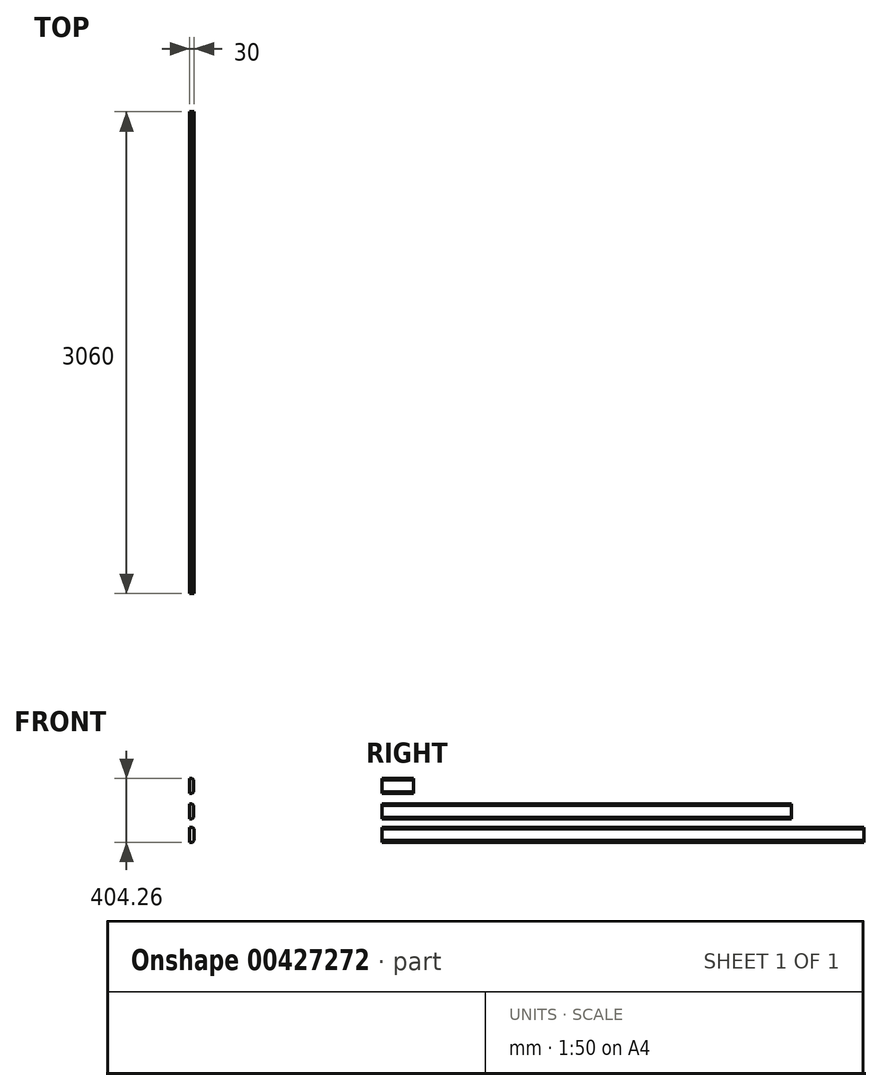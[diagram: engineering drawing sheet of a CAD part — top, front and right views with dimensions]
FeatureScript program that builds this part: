
annotation { "Feature Type Name" : "Feature", "Feature Type Description" : "" }
export const myFeature = defineFeature(function(context is Context, id is Id, definition is map)
    precondition{}
    {
        {
            var Q0;
            Q0=qCreatedBy(makeId("Right.planeOp"),FACE);
            var sketch = newSketch(context, id + "F0", { "sketchPlane" : qUnion([Q0])});
            skLineSegment(sketch, "E0.bottom", {"start": v(0, 0) * mm, "end": v(3060, 0) * mm});
            skLineSegment(sketch, "E0.top", {"start": v(0, 95) * mm, "end": v(3060, 95) * mm});
            skLineSegment(sketch, "E0.left", {"start": v(0, 0) * mm, "end": v(0, 95) * mm});
            skLineSegment(sketch, "E0.right", {"start": v(3060, 0) * mm, "end": v(3060, 95) * mm});
            skSolve(sketch);
        }
        {
            var Q0;
            Q0 = qSketchRegion(id + "F0", true);
            extrude(context, id + "F1", {"entities" : qUnion([Q0]), "depth" : 30 * mm, "offsetDistance" : 25 * mm});
        }
        {
            var Q0;
            Q0=makeQuery(id+"F1.opExtrude","CAP_EDGE",EDGE,{"disambiguationData":[OSD([sQuery(id+"F0.wireOp",EDGE,"E0.top")])],"isStart":false});
            var Q1;
            Q1=makeQuery(id+"F1.opExtrude","CAP_EDGE",EDGE,{"disambiguationData":[OSD([sQuery(id+"F0.wireOp",EDGE,"E0.bottom")])],"isStart":false});
            chamfer(context, id + "F2", {"entities" : qUnion([Q0, Q1]), "width" : 10 * mm, "tangentPropagation" : true});
        }
        {
            var Q0;
            Q0=qCreatedBy(makeId("Right.planeOp"),FACE);
            var sketch = newSketch(context, id + "F3", { "sketchPlane" : qUnion([Q0])});
            skLineSegment(sketch, "E1.bottom", {"start": v(0, 147.75) * mm, "end": v(2600, 147.75) * mm});
            skLineSegment(sketch, "E1.top", {"start": v(0, 242.75) * mm, "end": v(2600, 242.75) * mm});
            skLineSegment(sketch, "E1.left", {"start": v(0, 147.75) * mm, "end": v(0, 242.75) * mm});
            skLineSegment(sketch, "E1.right", {"start": v(2600, 147.75) * mm, "end": v(2600, 242.75) * mm});
            skSolve(sketch);
        }
        {
            var Q0;
            Q0 = qSketchRegion(id + "F3", true);
            extrude(context, id + "F4", {"entities" : qUnion([Q0]), "depth" : 25 * mm, "offsetDistance" : 25 * mm});
        }
        {
            var Q0;
            Q0=makeQuery(id+"F4.opExtrude","CAP_EDGE",EDGE,{"disambiguationData":[OSD([sQuery(id+"F3.wireOp",EDGE,"E1.bottom")])],"isStart":false});
            var Q1;
            Q1=makeQuery(id+"F4.opExtrude","CAP_EDGE",EDGE,{"disambiguationData":[OSD([sQuery(id+"F3.wireOp",EDGE,"E1.top")])],"isStart":false});
            chamfer(context, id + "F5", {"entities" : qUnion([Q0, Q1]), "width" : 10 * mm, "tangentPropagation" : true});
        }
        {
            var Q0;
            Q0=qCreatedBy(makeId("Right.planeOp"),FACE);
            var sketch = newSketch(context, id + "F6", { "sketchPlane" : qUnion([Q0])});
            skLineSegment(sketch, "E2.bottom", {"start": v(0, 309.26) * mm, "end": v(200, 309.26) * mm});
            skLineSegment(sketch, "E2.top", {"start": v(0, 404.26) * mm, "end": v(200, 404.26) * mm});
            skLineSegment(sketch, "E2.left", {"start": v(0, 309.26) * mm, "end": v(0, 404.26) * mm});
            skLineSegment(sketch, "E2.right", {"start": v(200, 309.26) * mm, "end": v(200, 404.26) * mm});
            skSolve(sketch);
        }
        {
            var Q0;
            Q0 = qSketchRegion(id + "F6", true);
            extrude(context, id + "F7", {"entities" : qUnion([Q0]), "depth" : 25 * mm, "offsetDistance" : 25 * mm});
        }
        {
            var Q0;
            Q0=makeQuery(id+"F7.opExtrude","CAP_EDGE",EDGE,{"disambiguationData":[OSD([sQuery(id+"F6.wireOp",EDGE,"E2.bottom")])],"isStart":false});
            var Q1;
            Q1=makeQuery(id+"F7.opExtrude","CAP_EDGE",EDGE,{"disambiguationData":[OSD([sQuery(id+"F6.wireOp",EDGE,"E2.top")])],"isStart":false});
            chamfer(context, id + "F8", {"entities" : qUnion([Q0, Q1]), "width" : 10 * mm, "tangentPropagation" : true});
        }
    });
